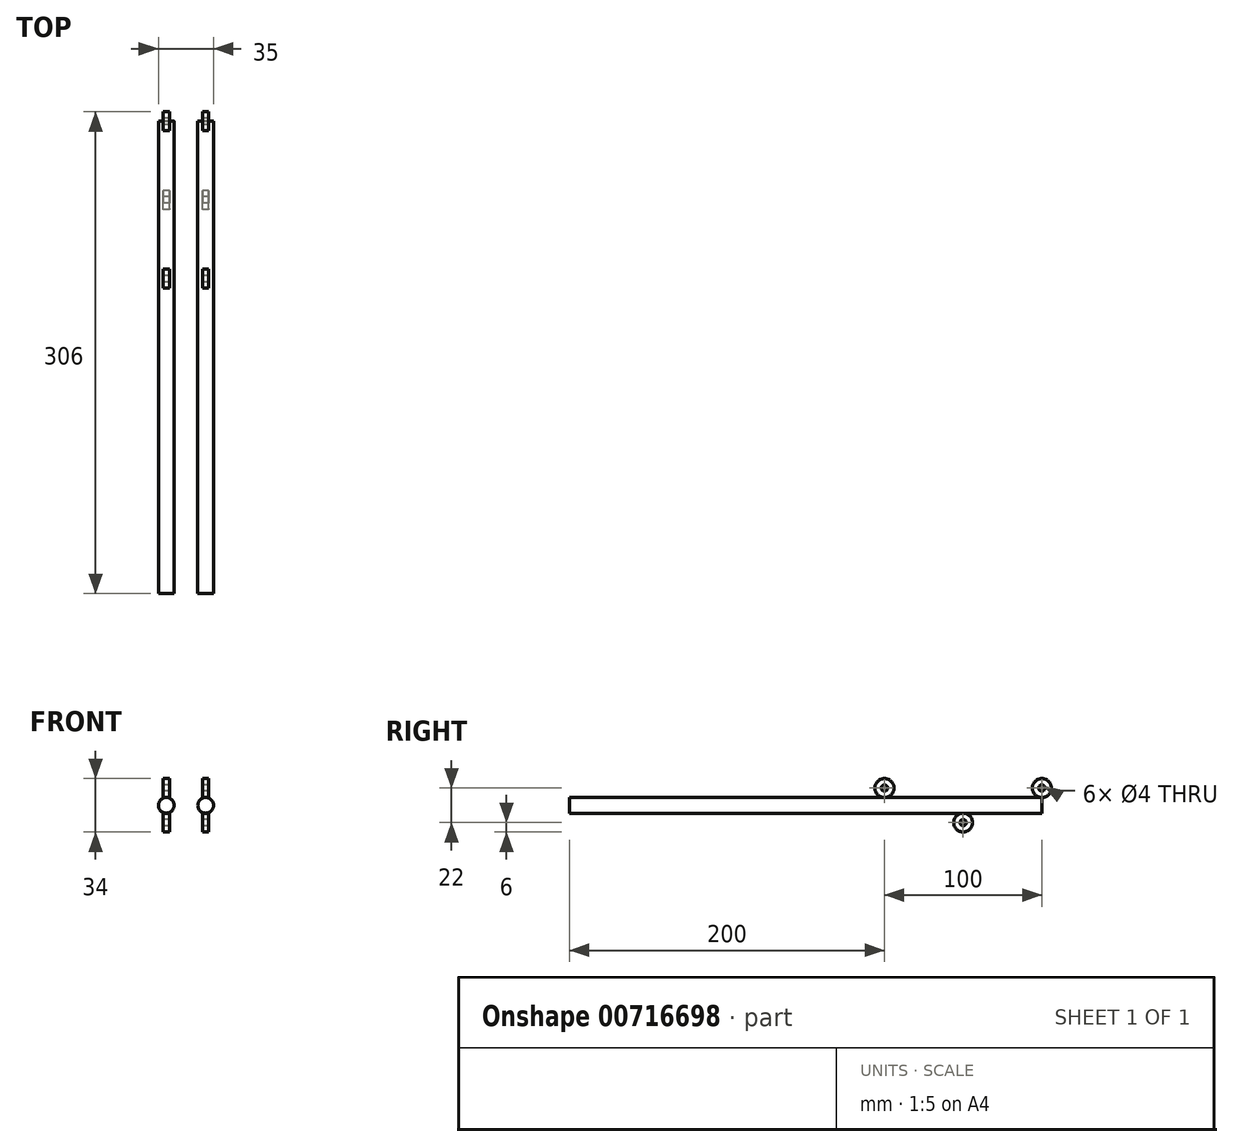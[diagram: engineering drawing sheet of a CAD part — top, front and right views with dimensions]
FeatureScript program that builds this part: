
annotation { "Feature Type Name" : "Feature", "Feature Type Description" : "" }
export const myFeature = defineFeature(function(context is Context, id is Id, definition is map)
    precondition{}
    {
        {
            assignVariable(context, id + "F0", {"name" : "Dia_Y_Wellen", "anyValue" : 10});
        }
        {
            assignVariable(context, id + "F1", {"name" : "Laenge_Y_Wellen", "anyValue" : 300});
        }
        {
            assignVariable(context, id + "F2", {"name" : "Abstand_Y_Wellen", "anyValue" : 100});
        }
        {
            var Q0;
            Q0=qCreatedBy(makeId("Front.planeOp"),FACE);
            var sketch = newSketch(context, id + "F3", { "sketchPlane" : qUnion([Q0])});
            skCircle(sketch, "E0", {"center": v(0, 0) * mm, "radius": 5 * mm});
            skSolve(sketch);
        }
        {
            var Q0;
            Q0=makeQuery(id+"F3.imprint","IMPRINT",FACE,{"disambiguationData":[TD([[makeQuery(id+"F3.imprint","IMPRINT",EDGE,{"derivedFrom":sQuery(id+"F3.wireOp",EDGE,"E0")}),1.0]])]});
            extrude(context, id + "F4", {"entities" : qUnion([Q0]), "depth" : (getVariable(context, 'Laenge_Y_Wellen')) * mm, "offsetDistance" : 25 * mm});
        }
        {
            var Q0;
            Q0=makeQuery(id+"F4.opExtrude","SWEPT_BODY",BODY,{"disambiguationData":[OSD([sQuery(id+"F3.wireOp",EDGE,"E0")])]});
            transform(context, id + "F5", {"entities" : qUnion([Q0]), "transformType" : TransformType.TRANSLATION_3D, "dx" : (-getVariable(context, 'Abstand_Y_Wellen') / 2) * mm, "dy" : 0 * mm, "dz" : 0 * mm, "makeCopy" : false});
        }
        {
            assignVariable(context, id + "F6", {"name" : "KugellagerDiaAussen", "anyValue" : 12});
        }
        {
            assignVariable(context, id + "F7", {"name" : "KugellagerBreite", "anyValue" : 4});
        }
        {
            assignVariable(context, id + "F8", {"name" : "Abstand_Kugellager1_Kugellager2", "anyValue" : 100});
        }
        {
            var Q0;
            Q0=qCreatedBy(makeId("Right.planeOp"),FACE);
            var sketch = newSketch(context, id + "F9", { "sketchPlane" : qUnion([Q0])});
            skCircle(sketch, "E1", {"center": v(0, 0) * mm, "radius": 6 * mm});
            skCircle(sketch, "E2", {"center": v(0, 0) * mm, "radius": 2 * mm});
            skSolve(sketch);
        }
        {
            var Q0;
            Q0 = qSketchRegion(id + "F9", true);
            extrude(context, id + "F10", {"entities" : qUnion([Q0]), "endBound" : BoundingType.SYMMETRIC, "depth" : (getVariable(context, 'KugellagerBreite')) * mm, "offsetDistance" : 25 * mm});
        }
        {
            var Q0;
            Q0=makeQuery(id+"F10.opExtrude","SWEPT_BODY",BODY,{"disambiguationData":[OSD([sQuery(id+"F9.wireOp",EDGE,"E1"),sQuery(id+"F9.wireOp",EDGE,"E2")])]});
            transform(context, id + "F11", {"entities" : qUnion([Q0]), "transformType" : TransformType.TRANSLATION_3D, "dx" : -(getVariable(context, 'Abstand_Y_Wellen') / 2) * mm, "dy" : 0 * mm, "dz" : ((getVariable(context, 'Dia_Y_Wellen') + getVariable(context, 'KugellagerDiaAussen')) / 2) * mm, "makeCopy" : false});
        }
        {
            var Q0;
            Q0=makeQuery(id+"F10.opExtrude","SWEPT_BODY",BODY,{"disambiguationData":[OSD([sQuery(id+"F9.wireOp",EDGE,"E1"),sQuery(id+"F9.wireOp",EDGE,"E2")])]});
            transform(context, id + "F12", {"entities" : qUnion([Q0]), "transformType" : TransformType.TRANSLATION_3D, "dx" : 0 * mm, "dy" : -(getVariable(context, 'Abstand_Kugellager1_Kugellager2')) * mm, "dz" : 0 * mm, "makeCopy" : true});
        }
        {
            var Q0;
            Q0=makeQuery(id+"F10.opExtrude","SWEPT_BODY",BODY,{"disambiguationData":[OSD([sQuery(id+"F9.wireOp",EDGE,"E1"),sQuery(id+"F9.wireOp",EDGE,"E2")])]});
            transform(context, id + "F13", {"entities" : qUnion([Q0]), "transformType" : TransformType.TRANSLATION_3D, "dx" : 0 * mm, "dy" : -(getVariable(context, 'Abstand_Kugellager1_Kugellager2') / 2) * mm, "dz" : -(getVariable(context, 'Dia_Y_Wellen') + getVariable(context, 'KugellagerDiaAussen')) * mm, "makeCopy" : true});
        }
        {
            var Q0;
            Q0=makeQuery(id+"F4.opExtrude","SWEPT_BODY",BODY,{"disambiguationData":[OSD([sQuery(id+"F3.wireOp",EDGE,"E0")])]});
            var Q1;
            Q1=makeQuery(id+"F10.opExtrude","SWEPT_BODY",BODY,{"disambiguationData":[OSD([sQuery(id+"F9.wireOp",EDGE,"E1"),sQuery(id+"F9.wireOp",EDGE,"E2")])]});
            var Q2;
            Q2=makeQuery(id+"F12.opPattern","COPY",BODY,{"derivedFrom":makeQuery(id+"F10.opExtrude","SWEPT_BODY",BODY,{"disambiguationData":[OSD([sQuery(id+"F9.wireOp",EDGE,"E1"),sQuery(id+"F9.wireOp",EDGE,"E2")])]}),"instanceName":"1"});
            var Q3;
            Q3=makeQuery(id+"F13.opPattern","COPY",BODY,{"derivedFrom":makeQuery(id+"F10.opExtrude","SWEPT_BODY",BODY,{"disambiguationData":[OSD([sQuery(id+"F9.wireOp",EDGE,"E1"),sQuery(id+"F9.wireOp",EDGE,"E2")])]}),"instanceName":"1"});
            var Q4;
            Q4=qCreatedBy(makeId("Right.planeOp"),FACE);
            transform(context, id + "F14", {"entities" : qUnion([Q0, Q1, Q2, Q3]), "transformType" : TransformType.TRANSLATION_DISTANCE, "transformDirection" : qUnion([Q4]), "distance" : 25 * mm, "makeCopy" : true});
        }
    });
